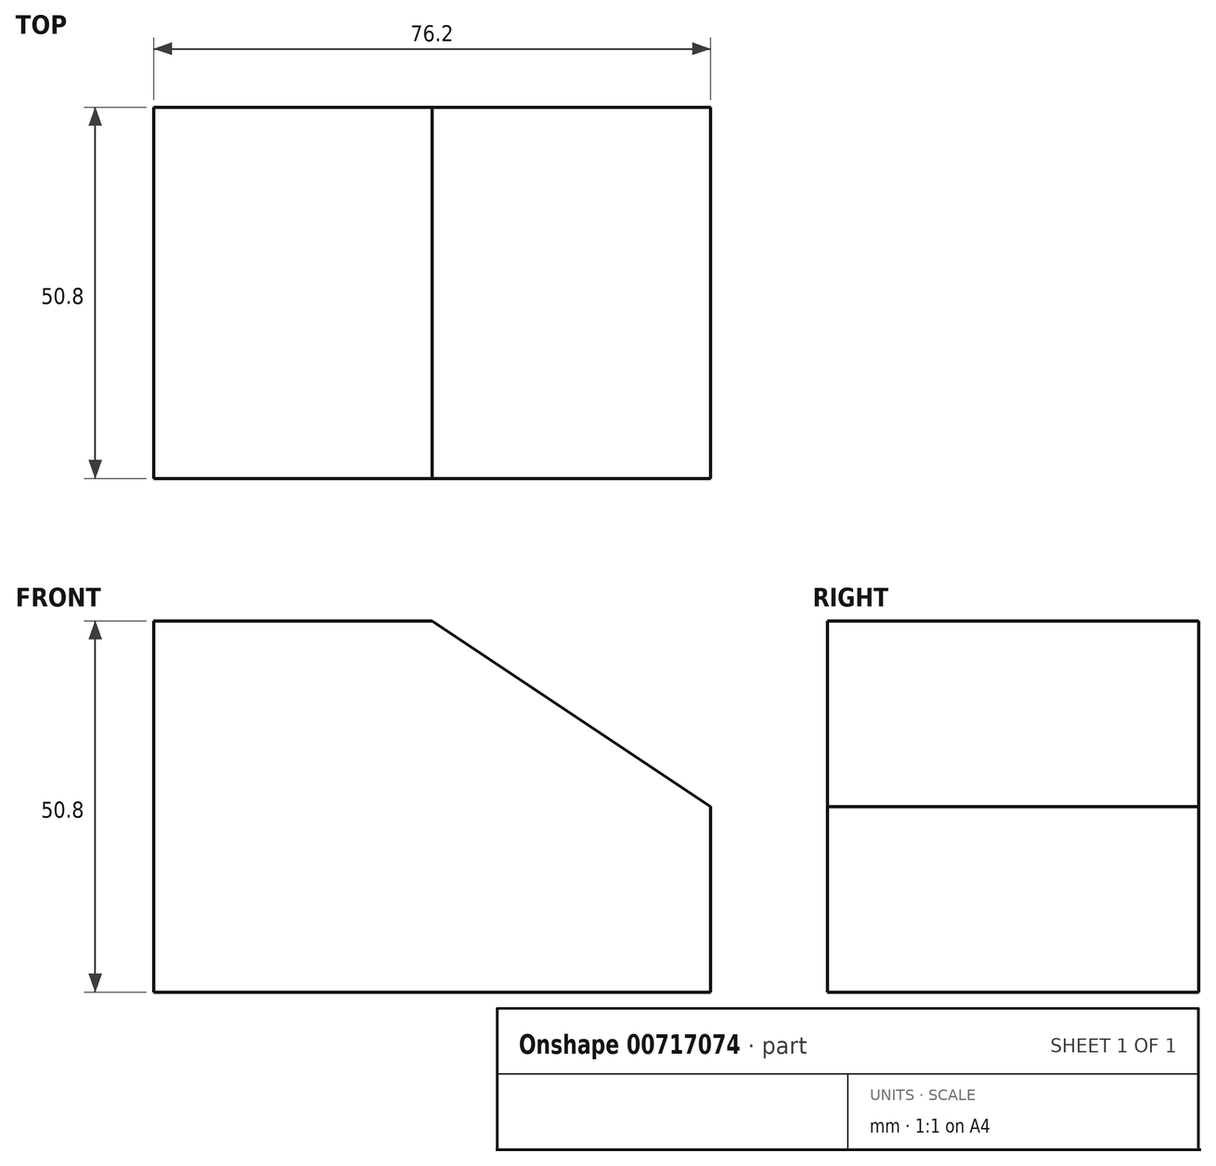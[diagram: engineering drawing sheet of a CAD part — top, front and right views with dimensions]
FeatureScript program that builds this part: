
annotation { "Feature Type Name" : "Feature", "Feature Type Description" : "" }
export const myFeature = defineFeature(function(context is Context, id is Id, definition is map)
    precondition{}
    {
        {
            var Q0;
            Q0=qCreatedBy(makeId("Front.planeOp"),FACE);
            var sketch = newSketch(context, id + "F0", { "sketchPlane" : qUnion([Q0])});
            skLineSegment(sketch, "E0", {"start": v(-38.1, -25.4) * mm, "end": v(38.1, -25.4) * mm});
            skLineSegment(sketch, "E1", {"start": v(-38.1, -25.4) * mm, "end": v(-38.1, 25.4) * mm});
            skLineSegment(sketch, "E2", {"start": v(-38.1, 25.4) * mm, "end": v(0, 25.4) * mm});
            skLineSegment(sketch, "E3", {"start": v(0, 25.4) * mm, "end": v(38.1, 0) * mm});
            skLineSegment(sketch, "E4", {"start": v(38.1, 0) * mm, "end": v(38.1, -25.4) * mm});
            skCircle(sketch, "E5", {"center": v(0, 0) * mm, "radius": 12.7 * mm});
            skSolve(sketch);
        }
        {
            var Q0;
            Q0=makeQuery(id+"F0.imprint","IMPRINT",FACE,{"disambiguationData":[TD([[makeQuery(id+"F0.imprint","IMPRINT",EDGE,{"derivedFrom":sQuery(id+"F0.wireOp",EDGE,"E5")}),1.0]])]});
            var Q1;
            Q1=makeQuery(id+"F0.imprint","IMPRINT",FACE,{"disambiguationData":[TD([[makeQuery(id+"F0.imprint","IMPRINT",EDGE,{"derivedFrom":sQuery(id+"F0.wireOp",EDGE,"E0")}),1.0]])]});
            extrude(context, id + "F1", {"entities" : qUnion([Q0, Q1]), "endBound" : BoundingType.SYMMETRIC, "depth" : 50.8 * mm, "offsetDistance" : 25.4 * mm});
        }
        {
            var Q0;
            Q0=sQuery(id+"F0.wireOp",EDGE,"E5");
            extrude(context, id + "F2", {"bodyType" : ToolBodyType.SURFACE, "surfaceEntities" : qUnion([Q0]), "endBound" : BoundingType.SYMMETRIC, "depth" : 50.8 * mm, "offsetDistance" : 25.4 * mm});
        }
    });
